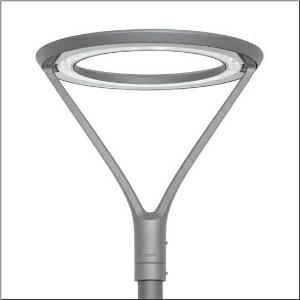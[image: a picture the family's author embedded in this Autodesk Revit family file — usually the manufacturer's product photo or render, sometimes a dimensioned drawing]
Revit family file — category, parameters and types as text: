
# Revit family: dl_r__20___st1_2a_5xa512836a008_c857
name_source: partatom
category: Lighting Fixtures
units: mm (PartAtom-declared; Revit-internal decimal feet)

## family parameters
Cut with Voids When Loaded = No
Host = Face
Light Source = No
Part Type = Normal
Room Calculation Point = No
Round Connector Dimension = Use Diameter
Shared = No

## types (1)
- --- (1 x LED, 3020 lm, 28.6 W, 2700K)
    Apparent Load = 29 VA
    CIE Flux Codes = 32 72 97 100 100
    Color Rendering = 70
    Color Temperature = 2700K
    Default Elevation = 1800 mm
    Description = DL® 20, mast luminaire, primary light control with reflector, highly specular, primary optical cover: cover, of toughened safety glass of clear glass with excellent transmission level, light distribution: ST1.2a, light emission: direct distribution, primary light characteristic: asymmetric, installation type: post-top, LED, High Power LED, rated luminous flux: 3.020lm, luminous efficacy: 106lm/W, light colour: 727, colour temperature: 2700K, control gear: Plus, control: flexible luminous flux parameterisation, time-dependent luminous flux control, constant luminous flux control, digital communication interface, power reduction, overheat protection, electronic power reduction, mains connection: 220..240V, 50/60Hz, connection cable pre-assembled, cable length: 5m, start of lifetime: 29W, end of service life: 29W, reduction: 15W, luminaire housing, upper part, of cast aluminium, powder-coated, Siteco® metallic grey (DB 702S), diameter: 690mm, height: 690mm, spigot size: 76mm (post-top), mounting height: 4..6m, luminaire housing, of cast aluminium, powder-coated, Siteco® metallic grey (DB 702S), equipment: standard, protection rating (complete): IP66, insulation class (complete): insulation class II (safety insulation), certification: CE, ENEC, VDE, impact resistance: IK08, permissible operating ambient temperature: -25..+35°C, standard-compliant lighting for roads and squares, packaging unit: 1 piece

Light Distribution: ST1.2a
    Height = 690 mm
    Lamp = 1 x LED
    Lamp Light Flux = 3020 lm
    Lamp Power = 28.6 W
    Lamp count = 1
    Length = 690 mm
    Luminous efficacy = 106 lm/W
    Manufacturer = Siteco
    ModVariant = No
    Model = 5XA512836A008
    Number of Poles = 1
    OnlyDefault = Yes
    Power Factor = 1
    Product Name = DL® 20 | ST1.2a
    Product group = mast luminaire | pylon top
    ProductGroupID = 6100
    Protection Class = Protection class II
    Protection Degree = IP 66
    RLX_Detail_Level = 1
    RLX_Emergency_Light_Flux = 0 lm
    RLX_Emergency_Type = 0
    RLX_Emergency_Type_DB = No
    RlxData = <blob elided: 206929 chars, md5=f79e5b4d>
    Socket = socket
    Standby Power = 0 W
    System Light Flux = 3020 lm
    System Power = 29 W
    Type Comments = factory setting: luminous flux: 100 % | dim-lin: 254 | 386 mA
    Type Image = l_1006001.jpg
    URL = http://relux.com
    VarID = @adj_098865
    Voltage = 0 V
    Weight = 0.00 kg
    Width = 0 mm  [stored 0 ft]

note: [stored X ft] marks values corroborated as IEEE doubles in the binary element streams (Revit-internal decimal feet)

## geometry (parser evidence)
native form markers: Blend x4, Sweep x10
no freeform markers — native parametric forms only
